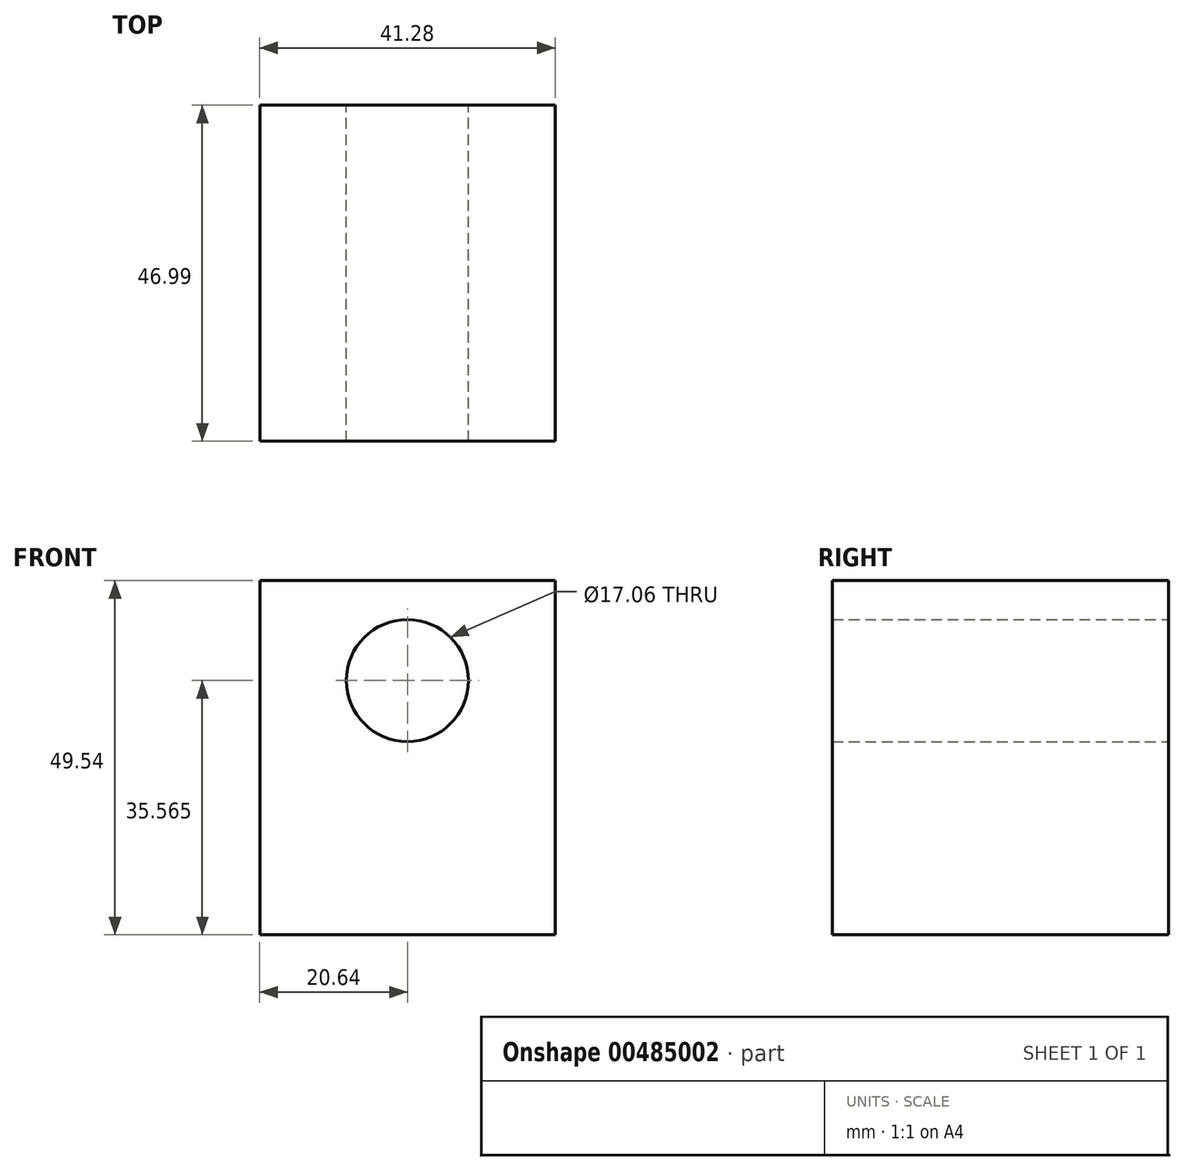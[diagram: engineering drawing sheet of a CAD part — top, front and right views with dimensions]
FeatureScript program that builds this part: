
annotation { "Feature Type Name" : "Feature", "Feature Type Description" : "" }
export const myFeature = defineFeature(function(context is Context, id is Id, definition is map)
    precondition{}
    {
        {
            var Q0;
            Q0=qCreatedBy(makeId("Front.planeOp"),FACE);
            var sketch = newSketch(context, id + "F0", { "sketchPlane" : qUnion([Q0])});
            skLineSegment(sketch, "E0.bottom", {"start": v(20.64, -24.77) * mm, "end": v(-20.64, -24.77) * mm});
            skLineSegment(sketch, "E0.top", {"start": v(20.64, 24.77) * mm, "end": v(-20.64, 24.77) * mm});
            skLineSegment(sketch, "E0.left", {"start": v(20.64, -24.77) * mm, "end": v(20.64, 24.77) * mm});
            skLineSegment(sketch, "E0.right", {"start": v(-20.64, -24.77) * mm, "end": v(-20.64, 24.77) * mm});
            skPoint(sketch, "E0.middle", {"position": v(0, 0) * mm});
            skLineSegment(sketch, "E1", {"start": v(0, 0) * mm, "end": v(0, 2.27) * mm});
            skCircle(sketch, "E2", {"center": v(0, 10.8) * mm, "radius": 8.53 * mm});
            skPoint(sketch, "E3.orphan", {"position": v(20.64, 10.8) * mm});
            skPoint(sketch, "E4.orphan", {"position": v(-20.64, 10.8) * mm});
            skPoint(sketch, "E5.orphan", {"position": v(0, 24.77) * mm});
            skSolve(sketch);
        }
        {
            var Q0;
            Q0=makeQuery(id+"F0.imprint","IMPRINT",FACE,{"disambiguationData":[TD([[makeQuery(id+"F0.imprint","IMPRINT",EDGE,{"derivedFrom":sQuery(id+"F0.wireOp",EDGE,"E0.bottom")}),-1.0]])]});
            extrude(context, id + "F1", {"entities" : qUnion([Q0]), "depth" : 47 * mm});
        }
    });
